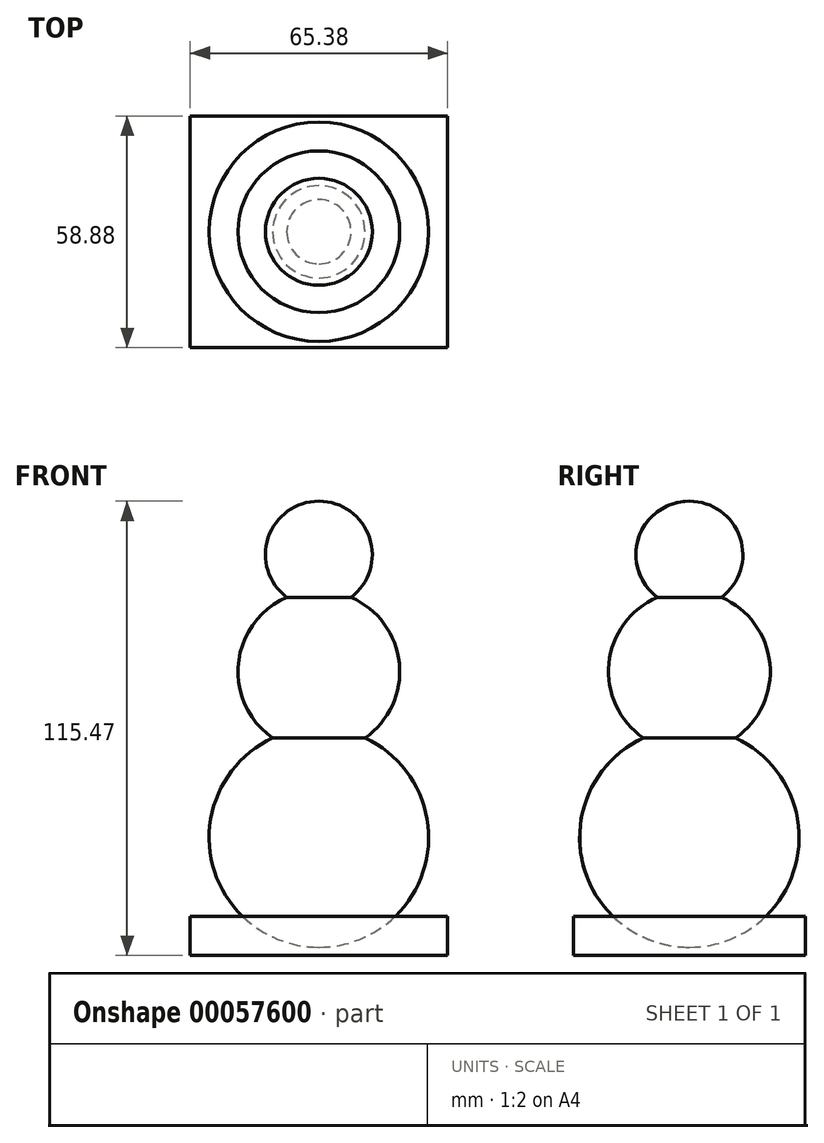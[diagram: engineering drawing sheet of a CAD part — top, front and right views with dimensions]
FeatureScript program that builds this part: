
annotation { "Feature Type Name" : "Feature", "Feature Type Description" : "" }
export const myFeature = defineFeature(function(context is Context, id is Id, definition is map)
    precondition{}
    {
        {
            var Q0;
            Q0=qCreatedBy(makeId("Right.planeOp"),FACE);
            var sketch = newSketch(context, id + "F0", { "sketchPlane" : qUnion([Q0])});
            skArc(sketch, "E0", {"start": v(0, -27.88) * mm, "mid": v(-27.88, 0) * mm, "end": v(0, 27.88) * mm});
            skLineSegment(sketch, "E1", {"start": v(0, 64.63) * mm, "end": v(0, 36.37) * mm});
            skLineSegment(sketch, "E2", {"start": v(0, 27.88) * mm, "end": v(0, -27.88) * mm});
            skArc(sketch, "E3", {"start": v(0, 21.62) * mm, "mid": v(-20.54, 42.17) * mm, "end": v(0, 62.71) * mm});
            skLineSegment(sketch, "E4", {"start": v(0, 62.71) * mm, "end": v(0, 21.62) * mm});
            skLineSegment(sketch, "E5", {"start": v(0, 85.47) * mm, "end": v(0, 58.3) * mm});
            skArc(sketch, "E6", {"start": v(0, 85.47) * mm, "mid": v(-13.58, 71.88) * mm, "end": v(0, 58.3) * mm});
            skSolve(sketch);
        }
        {
            var Q0;
            Q0=qCreatedBy(makeId("Right.planeOp"),FACE);
            var sketch = newSketch(context, id + "F1", { "sketchPlane" : qUnion([Q0])});
            skLineSegment(sketch, "E7", {"start": v(0, 0) * mm, "end": v(0, 53.14) * mm});
            skSolve(sketch);
        }
        {
            var Q0;
            Q0 = qSketchRegion(id + "F0", true);
            var Q1;
            Q1=sQuery(id+"F1.wireOp",EDGE,"E7");
            revolve(context, id + "F2", {"entities" : qUnion([Q0]), "axis" : qUnion([Q1]), "revolveType" : RevolveType.FULL});
        }
        {
            var Q0;
            Q0=qCreatedBy(makeId("Top.planeOp"),FACE);
            var sketch = newSketch(context, id + "F3", { "sketchPlane" : qUnion([Q0])});
            skLineSegment(sketch, "E8.rect.bottom", {"start": v(-32.7, 29.44) * mm, "end": v(32.7, 29.44) * mm});
            skLineSegment(sketch, "E8.rect.top", {"start": v(-32.7, -29.44) * mm, "end": v(32.7, -29.44) * mm});
            skLineSegment(sketch, "E8.rect.left", {"start": v(-32.7, 29.44) * mm, "end": v(-32.7, -29.44) * mm});
            skLineSegment(sketch, "E8.rect.right", {"start": v(32.7, 29.44) * mm, "end": v(32.7, -29.44) * mm});
            skPoint(sketch, "E8.rect.middle", {"position": v(0, 0) * mm});
            skSolve(sketch);
        }
        {
            var Q0;
            Q0 = qSketchRegion(id + "F3", true);
            extrude(context, id + "F4", {"entities" : qUnion([Q0]), "depth" : 10 * mm});
        }
        {
            var Q0;
            Q0=makeQuery(id+"F4.opExtrude","SWEPT_BODY",BODY,{"disambiguationData":[OSD([sQuery(id+"F3.wireOp",EDGE,"E8.rect.bottom"),sQuery(id+"F3.wireOp",EDGE,"E8.rect.top"),sQuery(id+"F3.wireOp",EDGE,"E8.rect.left"),sQuery(id+"F3.wireOp",EDGE,"E8.rect.right")])]});
            transform(context, id + "F5", {"entities" : qUnion([Q0]), "transformType" : TransformType.TRANSLATION_3D, "dx" : 0 * mm, "dy" : 0 * mm, "dz" : -30 * mm, "makeCopy" : false});
        }
    });
